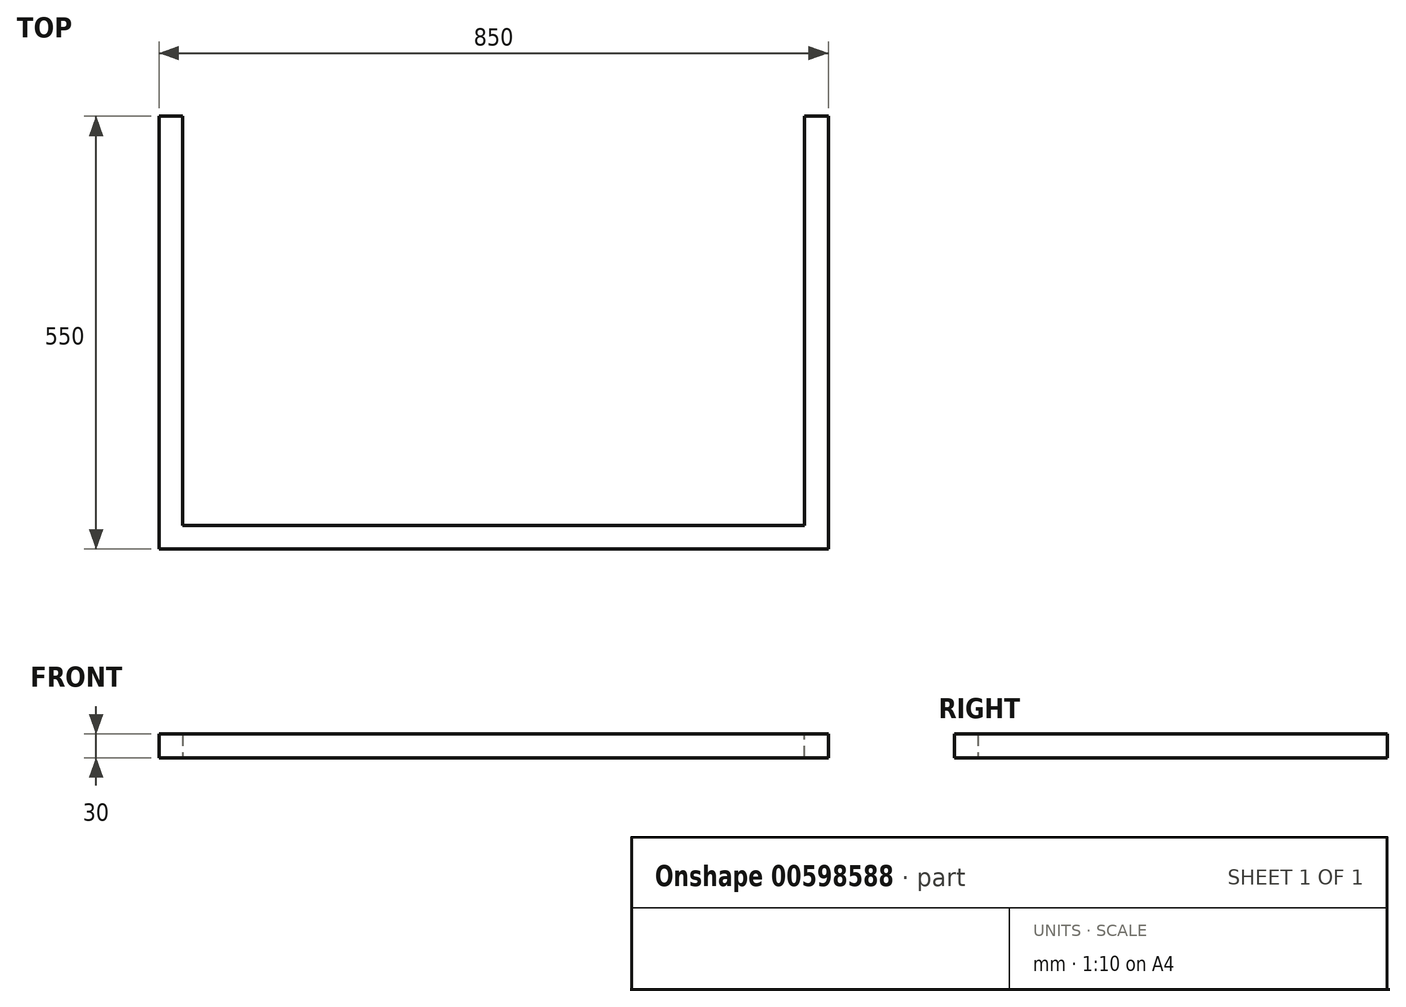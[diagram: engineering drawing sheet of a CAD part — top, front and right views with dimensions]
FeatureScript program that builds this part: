
annotation { "Feature Type Name" : "Feature", "Feature Type Description" : "" }
export const myFeature = defineFeature(function(context is Context, id is Id, definition is map)
    precondition{}
    {
        {
            var Q0;
            Q0=qCreatedBy(makeId("Front.planeOp"),FACE);
            var sketch = newSketch(context, id + "F0", { "sketchPlane" : qUnion([Q0])});
            skLineSegment(sketch, "E0.bottom", {"start": v(-15, 15) * mm, "end": v(15, 15) * mm});
            skLineSegment(sketch, "E0.top", {"start": v(-15, -15) * mm, "end": v(15, -15) * mm});
            skLineSegment(sketch, "E0.left", {"start": v(-15, 15) * mm, "end": v(-15, -15) * mm});
            skLineSegment(sketch, "E0.right", {"start": v(15, 15) * mm, "end": v(15, -15) * mm});
            skSolve(sketch);
        }
        {
            var Q0;
            Q0=makeQuery(id+"F0.imprint","IMPRINT",FACE,{"disambiguationData":[TD([[makeQuery(id+"F0.imprint","IMPRINT",EDGE,{"derivedFrom":sQuery(id+"F0.wireOp",EDGE,"E0.bottom")}),-1.0]])]});
            extrude(context, id + "F1", {"entities" : qUnion([Q0]), "endBound" : BoundingType.SYMMETRIC, "depth" : 550 * mm, "offsetDistance" : 25 * mm});
        }
        {
            var Q0;
            Q0=makeQuery(id+"F1.opExtrude","SWEPT_FACE",FACE,{"disambiguationData":[OSD([sQuery(id+"F0.wireOp",EDGE,"E0.right")])]});
            var sketch = newSketch(context, id + "F2", { "sketchPlane" : qUnion([Q0])});
            skLineSegment(sketch, "E1.bottom", {"start": v(-275, 15) * mm, "end": v(-245, 15) * mm});
            skLineSegment(sketch, "E1.top", {"start": v(-275, -15) * mm, "end": v(-245, -15) * mm});
            skLineSegment(sketch, "E1.left", {"start": v(-275, 15) * mm, "end": v(-275, -15) * mm});
            skLineSegment(sketch, "E1.right", {"start": v(-245, 15) * mm, "end": v(-245, -15) * mm});
            skSolve(sketch);
        }
        {
            var Q0;
            Q0=makeQuery(id+"F2.imprint","IMPRINT",FACE,{"disambiguationData":[TD([[makeQuery(id+"F2.imprint","IMPRINT",EDGE,{"derivedFrom":sQuery(id+"F2.wireOp",EDGE,"E1.bottom")}),-1.0]])]});
            extrude(context, id + "F3", {"entities" : qUnion([Q0]), "operationType" : NewBodyOperationType.ADD, "depth" : 820 * mm, "offsetDistance" : 25 * mm});
        }
        {
            var Q0;
            Q0=makeQuery(id+"F3.opExtrude","SWEPT_FACE",FACE,{"disambiguationData":[OSD([sQuery(id+"F2.wireOp",EDGE,"E1.right")])]});
            var sketch = newSketch(context, id + "F4", { "sketchPlane" : qUnion([Q0])});
            skLineSegment(sketch, "E2.bottom", {"start": v(-835, 15) * mm, "end": v(-805, 15) * mm});
            skLineSegment(sketch, "E2.top", {"start": v(-835, -15) * mm, "end": v(-805, -15) * mm});
            skLineSegment(sketch, "E2.left", {"start": v(-835, 15) * mm, "end": v(-835, -15) * mm});
            skLineSegment(sketch, "E2.right", {"start": v(-805, 15) * mm, "end": v(-805, -15) * mm});
            skSolve(sketch);
        }
        {
            var Q0;
            Q0=makeQuery(id+"F4.imprint","IMPRINT",FACE,{"disambiguationData":[TD([[makeQuery(id+"F4.imprint","IMPRINT",EDGE,{"derivedFrom":sQuery(id+"F4.wireOp",EDGE,"E2.bottom")}),-1.0]])]});
            var Q1;
            Q1=makeQuery(id+"F1.opExtrude","CAP_FACE",FACE,{"disambiguationData":[OSD([sQuery(id+"F0.wireOp",EDGE,"E0.bottom"),sQuery(id+"F0.wireOp",EDGE,"E0.top"),sQuery(id+"F0.wireOp",EDGE,"E0.left"),sQuery(id+"F0.wireOp",EDGE,"E0.right")])],"isStart":true});
            extrude(context, id + "F5", {"entities" : qUnion([Q0]), "operationType" : NewBodyOperationType.ADD, "endBound" : BoundingType.UP_TO_SURFACE, "depth" : 25 * mm, "endBoundEntityFace" : qUnion([Q1]), "offsetDistance" : 25 * mm, "hasSecondDirection" : true, "secondDirectionOppositeDirection" : true, "secondDirectionDepth" : 25 * mm});
        }
    });
